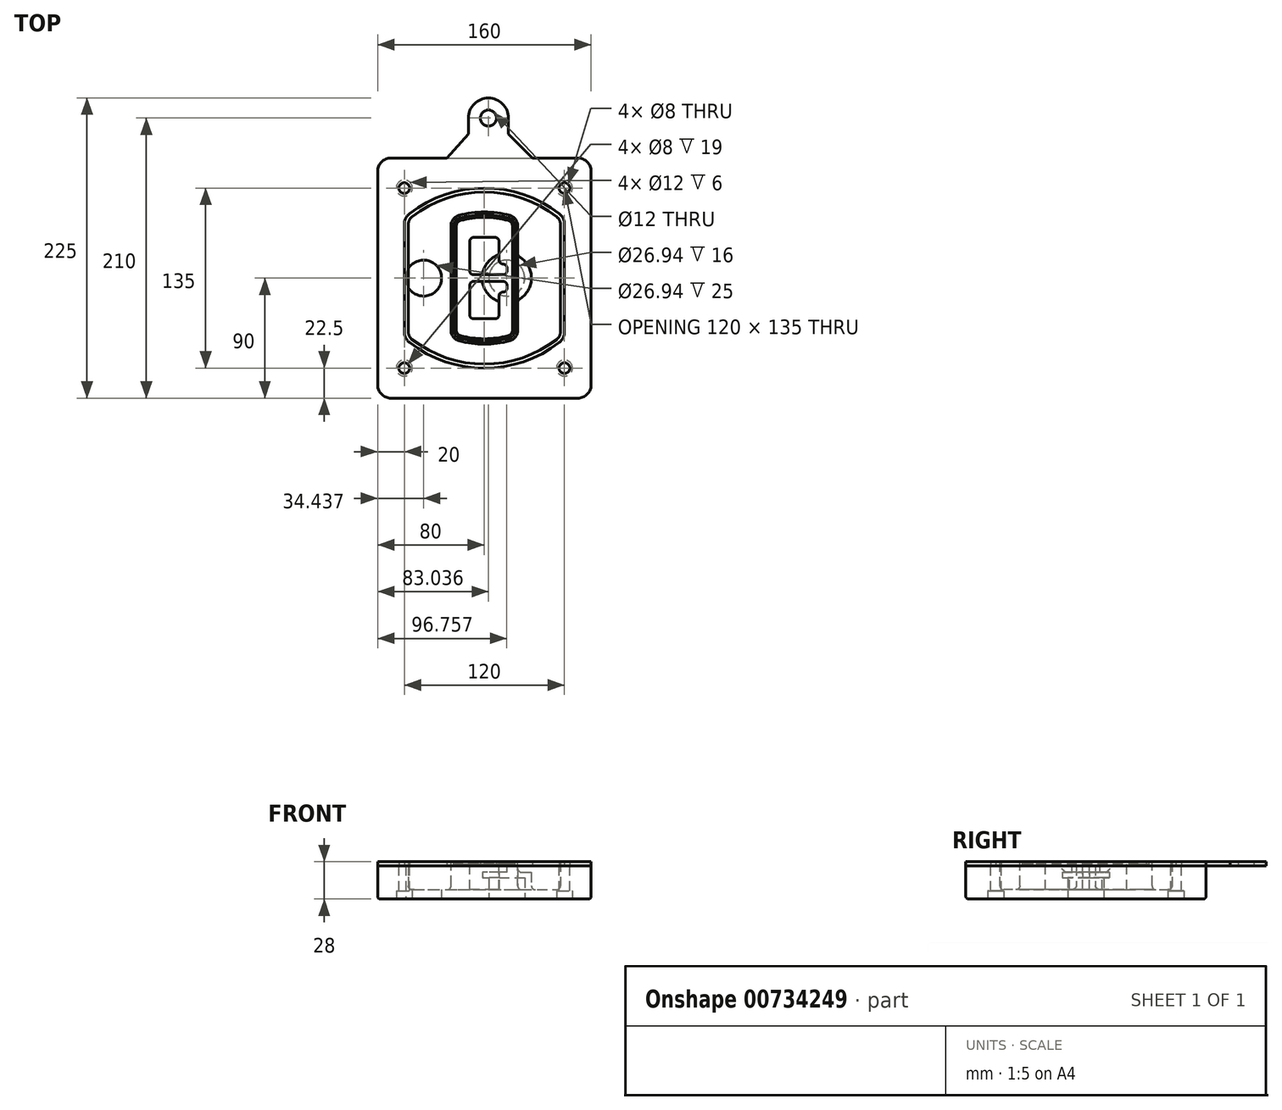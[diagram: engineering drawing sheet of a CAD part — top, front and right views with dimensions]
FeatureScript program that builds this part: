
annotation { "Feature Type Name" : "Feature", "Feature Type Description" : "" }
export const myFeature = defineFeature(function(context is Context, id is Id, definition is map)
    precondition{}
    {
        {
            var Q0;
            Q0=qCreatedBy(makeId("Top.planeOp"),FACE);
            var sketch = newSketch(context, id + "F0", { "sketchPlane" : qUnion([Q0])});
            skPoint(sketch, "E0.rect.middle", {"position": v(0, 0) * mm});
            skLineSegment(sketch, "E1.bottom", {"start": v(-70, -90) * mm, "end": v(70, -90) * mm});
            skLineSegment(sketch, "E1.top", {"start": v(-70, 90) * mm, "end": v(70, 90) * mm});
            skLineSegment(sketch, "E1.left", {"start": v(-80, -80) * mm, "end": v(-80, 80) * mm});
            skLineSegment(sketch, "E1.right", {"start": v(80, -80) * mm, "end": v(80, 80) * mm});
            skLineSegment(sketch, "E2", {"start": v(-80, 90) * mm, "end": v(80, -90) * mm, "construction": true});
            skLineSegment(sketch, "E3", {"start": v(80, 90) * mm, "end": v(-80, -90) * mm, "construction": true});
            skCircle(sketch, "E4", {"center": v(-60, 67.5) * mm, "radius": 4 * mm});
            skCircle(sketch, "E5", {"center": v(60, 67.5) * mm, "radius": 4 * mm});
            skCircle(sketch, "E6", {"center": v(60, -67.5) * mm, "radius": 4 * mm});
            skCircle(sketch, "E7", {"center": v(-60, -67.5) * mm, "radius": 4 * mm});
            skLineSegment(sketch, "E8", {"start": v(-60, 67.5) * mm, "end": v(60, 67.5) * mm, "construction": true});
            skLineSegment(sketch, "E9", {"start": v(60, 67.5) * mm, "end": v(60, -67.5) * mm, "construction": true});
            skLineSegment(sketch, "E10", {"start": v(60, -67.5) * mm, "end": v(-60, -67.5) * mm, "construction": true});
            skLineSegment(sketch, "E11", {"start": v(-60, -67.5) * mm, "end": v(-60, 67.5) * mm, "construction": true});
            skLineSegment(sketch, "E12", {"start": v(-60, 40.3) * mm, "end": v(-60, -40.3) * mm});
            skLineSegment(sketch, "E13", {"start": v(60, 40.3) * mm, "end": v(60, -40.3) * mm});
            skArc(sketch, "E14", {"start": v(56.15, 48.18) * mm, "mid": v(0, 67.5) * mm, "end": v(-56.15, 48.18) * mm});
            skArc(sketch, "E15", {"start": v(-56.15, -48.18) * mm, "mid": v(0, -67.5) * mm, "end": v(56.15, -48.18) * mm});
            skLineSegment(sketch, "E16", {"start": v(-60, 0) * mm, "end": v(60, 0) * mm, "construction": true});
            skPoint(sketch, "E17.visualSharp", {"position": v(-60, -45) * mm});
            skArc(sketch, "E17.filletArc", {"start": v(-60, -40.3) * mm, "mid": v(-58.99, -44.68) * mm, "end": v(-56.15, -48.18) * mm});
            skPoint(sketch, "E18.visualSharp", {"position": v(-60, 45) * mm});
            skArc(sketch, "E18.filletArc", {"start": v(-56.15, 48.18) * mm, "mid": v(-58.99, 44.68) * mm, "end": v(-60, 40.3) * mm});
            skPoint(sketch, "E19.visualSharp", {"position": v(60, 45) * mm});
            skArc(sketch, "E19.filletArc", {"start": v(60, 40.3) * mm, "mid": v(58.99, 44.68) * mm, "end": v(56.15, 48.18) * mm});
            skPoint(sketch, "E20.visualSharp", {"position": v(60, -45) * mm});
            skArc(sketch, "E20.filletArc", {"start": v(56.15, -48.18) * mm, "mid": v(58.99, -44.68) * mm, "end": v(60, -40.3) * mm});
            skPoint(sketch, "E21.visualSharp", {"position": v(-80, 90) * mm});
            skArc(sketch, "E21.filletArc", {"start": v(-70, 90) * mm, "mid": v(-77.07, 87.07) * mm, "end": v(-80, 80) * mm});
            skPoint(sketch, "E22.visualSharp", {"position": v(80, 90) * mm});
            skArc(sketch, "E22.filletArc", {"start": v(80, 80) * mm, "mid": v(77.07, 87.07) * mm, "end": v(70, 90) * mm});
            skPoint(sketch, "E23.visualSharp", {"position": v(80, -90) * mm});
            skArc(sketch, "E23.filletArc", {"start": v(70, -90) * mm, "mid": v(77.07, -87.07) * mm, "end": v(80, -80) * mm});
            skPoint(sketch, "E24.visualSharp", {"position": v(-80, -90) * mm});
            skArc(sketch, "E24.filletArc", {"start": v(-80, -80) * mm, "mid": v(-77.07, -87.07) * mm, "end": v(-70, -90) * mm});
            skArc(sketch, "E25.0", {"start": v(57, 40.3) * mm, "mid": v(56.3, 43.36) * mm, "end": v(54.3, 45.81) * mm});
            skLineSegment(sketch, "E25.1", {"start": v(57, 40.3) * mm, "end": v(57, -40.3) * mm});
            skArc(sketch, "E25.2", {"start": v(54.3, -45.81) * mm, "mid": v(56.3, -43.36) * mm, "end": v(57, -40.3) * mm});
            skArc(sketch, "E25.3", {"start": v(-54.3, -45.81) * mm, "mid": v(0, -64.5) * mm, "end": v(54.3, -45.81) * mm});
            skArc(sketch, "E25.4", {"start": v(-57, -40.3) * mm, "mid": v(-56.3, -43.36) * mm, "end": v(-54.3, -45.81) * mm});
            skArc(sketch, "E25.5", {"start": v(54.3, 45.81) * mm, "mid": v(0, 64.5) * mm, "end": v(-54.3, 45.81) * mm});
            skLineSegment(sketch, "E25.6", {"start": v(-57, 40.3) * mm, "end": v(-57, -40.3) * mm});
            skArc(sketch, "E25.7", {"start": v(-54.3, 45.81) * mm, "mid": v(-56.3, 43.36) * mm, "end": v(-57, 40.3) * mm});
            skArc(sketch, "E26.0", {"start": v(-58.62, 51.33) * mm, "mid": v(-62.58, 46.43) * mm, "end": v(-64, 40.3) * mm});
            skArc(sketch, "E26.1", {"start": v(58.62, 51.33) * mm, "mid": v(0, 71.5) * mm, "end": v(-58.62, 51.33) * mm});
            skArc(sketch, "E26.2", {"start": v(64, 40.3) * mm, "mid": v(62.58, 46.43) * mm, "end": v(58.62, 51.33) * mm});
            skLineSegment(sketch, "E26.3", {"start": v(64, 40.3) * mm, "end": v(64, -40.3) * mm});
            skArc(sketch, "E26.4", {"start": v(58.62, -51.33) * mm, "mid": v(62.58, -46.43) * mm, "end": v(64, -40.3) * mm});
            skLineSegment(sketch, "E26.5", {"start": v(-64, 40.3) * mm, "end": v(-64, -40.3) * mm});
            skArc(sketch, "E26.6", {"start": v(-58.62, -51.33) * mm, "mid": v(0, -71.5) * mm, "end": v(58.62, -51.33) * mm});
            skArc(sketch, "E26.7", {"start": v(-64, -40.3) * mm, "mid": v(-62.58, -46.43) * mm, "end": v(-58.62, -51.33) * mm});
            skSolve(sketch);
        }
        {
            var Q0;
            Q0=makeQuery(id+"F0.imprint","IMPRINT",FACE,{"disambiguationData":[TD([[makeQuery(id+"F0.imprint","IMPRINT",EDGE,{"derivedFrom":sQuery(id+"F0.wireOp",EDGE,"E1.bottom")}),1.0]])]});
            var Q1;
            Q1=makeQuery(id+"F0.imprint","IMPRINT",FACE,{"disambiguationData":[TD([[makeQuery(id+"F0.imprint","IMPRINT",EDGE,{"derivedFrom":sQuery(id+"F0.wireOp",EDGE,"E12")}),1.0]])]});
            var Q2;
            Q2=makeQuery(id+"F0.imprint","IMPRINT",FACE,{"disambiguationData":[TD([[makeQuery(id+"F0.imprint","IMPRINT",EDGE,{"derivedFrom":sQuery(id+"F0.wireOp",EDGE,"E25.0")}),1.0]])]});
            var Q3;
            Q3=makeQuery(id+"F0.imprint","IMPRINT",FACE,{"disambiguationData":[TD([[makeQuery(id+"F0.imprint","IMPRINT",EDGE,{"derivedFrom":sQuery(id+"F0.wireOp",EDGE,"E12")}),-1.0]])]});
            extrude(context, id + "F1", {"entities" : qUnion([Q0, Q1, Q2, Q3]), "oppositeDirection" : true, "depth" : 25 * mm});
        }
        {
            var Q0;
            Q0=makeQuery(id+"F0.imprint","IMPRINT",FACE,{"disambiguationData":[TD([[makeQuery(id+"F0.imprint","IMPRINT",EDGE,{"derivedFrom":sQuery(id+"F0.wireOp",EDGE,"E12")}),1.0]])]});
            extrude(context, id + "F2", {"entities" : qUnion([Q0]), "operationType" : NewBodyOperationType.ADD, "depth" : 3 * mm});
        }
        {
            var Q0;
            Q0=makeQuery(id+"F0.imprint","IMPRINT",FACE,{"disambiguationData":[TD([[makeQuery(id+"F0.imprint","IMPRINT",EDGE,{"derivedFrom":sQuery(id+"F0.wireOp",EDGE,"E25.0")}),1.0]])]});
            extrude(context, id + "F3", {"entities" : qUnion([Q0]), "operationType" : NewBodyOperationType.REMOVE, "oppositeDirection" : true, "depth" : 18 * mm});
        }
        {
            var Q0;
            Q0=makeQuery(id+"F2.opExtrude","CAP_FACE",FACE,{"disambiguationData":[OSD([sQuery(id+"F0.wireOp",EDGE,"E12"),sQuery(id+"F0.wireOp",EDGE,"E13"),sQuery(id+"F0.wireOp",EDGE,"E14"),sQuery(id+"F0.wireOp",EDGE,"E15"),sQuery(id+"F0.wireOp",EDGE,"E17.filletArc"),sQuery(id+"F0.wireOp",EDGE,"E18.filletArc"),sQuery(id+"F0.wireOp",EDGE,"E19.filletArc"),sQuery(id+"F0.wireOp",EDGE,"E20.filletArc"),sQuery(id+"F0.wireOp",EDGE,"E25.0"),sQuery(id+"F0.wireOp",EDGE,"E25.1"),sQuery(id+"F0.wireOp",EDGE,"E25.2"),sQuery(id+"F0.wireOp",EDGE,"E25.3"),sQuery(id+"F0.wireOp",EDGE,"E25.4"),sQuery(id+"F0.wireOp",EDGE,"E25.5"),sQuery(id+"F0.wireOp",EDGE,"E25.6"),sQuery(id+"F0.wireOp",EDGE,"E25.7")])],"isStart":false});
            var sketch = newSketch(context, id + "F4", { "sketchPlane" : qUnion([Q0])});
            skArc(sketch, "E27.0", {"start": v(-19.08, -46.97) * mm, "mid": v(0, -49.5) * mm, "end": v(19.08, -46.97) * mm});
            skArc(sketch, "E28.0", {"start": v(19.08, 46.97) * mm, "mid": v(0, 49.5) * mm, "end": v(-19.08, 46.97) * mm});
            skLineSegment(sketch, "E29", {"start": v(-25, 39.25) * mm, "end": v(-25, -39.25) * mm});
            skLineSegment(sketch, "E30", {"start": v(25, 39.25) * mm, "end": v(25, -39.25) * mm});
            skLineSegment(sketch, "E31", {"start": v(-25, 45.1) * mm, "end": v(25, 45.1) * mm, "construction": true});
            skLineSegment(sketch, "E32", {"start": v(-25, -45.1) * mm, "end": v(25, -45.1) * mm, "construction": true});
            skPoint(sketch, "E33.visualSharp", {"position": v(-25, 45.1) * mm});
            skArc(sketch, "E33.filletArc", {"start": v(-19.08, 46.97) * mm, "mid": v(-23.35, 44.11) * mm, "end": v(-25, 39.25) * mm});
            skPoint(sketch, "E34.visualSharp", {"position": v(25, 45.1) * mm});
            skArc(sketch, "E34.filletArc", {"start": v(25, 39.25) * mm, "mid": v(23.35, 44.11) * mm, "end": v(19.08, 46.97) * mm});
            skPoint(sketch, "E35.visualSharp", {"position": v(25, -45.1) * mm});
            skArc(sketch, "E35.filletArc", {"start": v(19.08, -46.97) * mm, "mid": v(23.35, -44.11) * mm, "end": v(25, -39.25) * mm});
            skPoint(sketch, "E36.visualSharp", {"position": v(-25, -45.1) * mm});
            skArc(sketch, "E36.filletArc", {"start": v(-25, -39.25) * mm, "mid": v(-23.35, -44.11) * mm, "end": v(-19.08, -46.97) * mm});
            skArc(sketch, "E37.0", {"start": v(54.3, 45.81) * mm, "mid": v(0, 64.5) * mm, "end": v(-54.3, 45.81) * mm});
            skArc(sketch, "E37.1", {"start": v(-54.3, 45.81) * mm, "mid": v(-56.3, 43.36) * mm, "end": v(-57, 40.3) * mm});
            skLineSegment(sketch, "E37.2", {"start": v(-57, 40.3) * mm, "end": v(-57, -40.3) * mm});
            skArc(sketch, "E37.3", {"start": v(-57, -40.3) * mm, "mid": v(-56.3, -43.36) * mm, "end": v(-54.3, -45.81) * mm});
            skArc(sketch, "E37.4", {"start": v(-54.3, -45.81) * mm, "mid": v(0, -64.5) * mm, "end": v(54.3, -45.81) * mm});
            skArc(sketch, "E37.5", {"start": v(54.3, -45.81) * mm, "mid": v(56.3, -43.36) * mm, "end": v(57, -40.3) * mm});
            skLineSegment(sketch, "E37.6", {"start": v(57, 40.3) * mm, "end": v(57, -40.3) * mm});
            skArc(sketch, "E37.7", {"start": v(57, 40.3) * mm, "mid": v(56.3, 43.36) * mm, "end": v(54.3, 45.81) * mm});
            skLineSegment(sketch, "E38.0", {"start": v(23, 39.25) * mm, "end": v(23, -39.25) * mm});
            skArc(sketch, "E38.1", {"start": v(18.56, -45.04) * mm, "mid": v(21.76, -42.9) * mm, "end": v(23, -39.25) * mm});
            skArc(sketch, "E38.2", {"start": v(-18.56, -45.04) * mm, "mid": v(0, -47.5) * mm, "end": v(18.56, -45.04) * mm});
            skArc(sketch, "E38.3", {"start": v(-23, -39.25) * mm, "mid": v(-21.76, -42.9) * mm, "end": v(-18.56, -45.04) * mm});
            skLineSegment(sketch, "E38.4", {"start": v(-23, 39.25) * mm, "end": v(-23, -39.25) * mm});
            skArc(sketch, "E38.5", {"start": v(23, 39.25) * mm, "mid": v(21.76, 42.9) * mm, "end": v(18.56, 45.04) * mm});
            skArc(sketch, "E38.6", {"start": v(-18.56, 45.04) * mm, "mid": v(-21.76, 42.9) * mm, "end": v(-23, 39.25) * mm});
            skArc(sketch, "E38.7", {"start": v(18.56, 45.04) * mm, "mid": v(0, 47.5) * mm, "end": v(-18.56, 45.04) * mm});
            skArc(sketch, "E39.0", {"start": v(21, 39.25) * mm, "mid": v(20.18, 41.68) * mm, "end": v(18.04, 43.1) * mm});
            skLineSegment(sketch, "E39.1", {"start": v(21, 39.25) * mm, "end": v(21, -39.25) * mm});
            skArc(sketch, "E39.2", {"start": v(18.04, -43.1) * mm, "mid": v(20.18, -41.68) * mm, "end": v(21, -39.25) * mm});
            skArc(sketch, "E39.3", {"start": v(-18.04, -43.1) * mm, "mid": v(0, -45.5) * mm, "end": v(18.04, -43.1) * mm});
            skArc(sketch, "E39.4", {"start": v(-21, -39.25) * mm, "mid": v(-20.18, -41.68) * mm, "end": v(-18.04, -43.1) * mm});
            skArc(sketch, "E39.5", {"start": v(18.04, 43.1) * mm, "mid": v(0, 45.5) * mm, "end": v(-18.04, 43.1) * mm});
            skLineSegment(sketch, "E39.6", {"start": v(-21, 39.25) * mm, "end": v(-21, -39.25) * mm});
            skArc(sketch, "E39.7", {"start": v(-18.04, 43.1) * mm, "mid": v(-20.18, 41.68) * mm, "end": v(-21, 39.25) * mm});
            skLineSegment(sketch, "E40", {"start": v(-25, 0) * mm, "end": v(25, 0) * mm, "construction": true});
            skLineSegment(sketch, "E41", {"start": v(-11, 5.5) * mm, "end": v(-11, 27.5) * mm});
            skLineSegment(sketch, "E42", {"start": v(-8, 30.5) * mm, "end": v(8, 30.5) * mm});
            skLineSegment(sketch, "E43", {"start": v(11, 27.5) * mm, "end": v(11, 13.5) * mm});
            skLineSegment(sketch, "E44", {"start": v(14, 10.5) * mm, "end": v(14, 10.5) * mm});
            skLineSegment(sketch, "E45", {"start": v(17, 7.5) * mm, "end": v(17, 5.5) * mm});
            skLineSegment(sketch, "E46", {"start": v(14, 2.5) * mm, "end": v(-8, 2.5) * mm});
            skPoint(sketch, "E47.visualSharp", {"position": v(-11, 30.5) * mm});
            skArc(sketch, "E47.filletArc", {"start": v(-8, 30.5) * mm, "mid": v(-10.12, 29.62) * mm, "end": v(-11, 27.5) * mm});
            skPoint(sketch, "E48.visualSharp", {"position": v(11, 30.5) * mm});
            skArc(sketch, "E48.filletArc", {"start": v(11, 27.5) * mm, "mid": v(10.12, 29.62) * mm, "end": v(8, 30.5) * mm});
            skPoint(sketch, "E49.visualSharp", {"position": v(11, 10.5) * mm});
            skArc(sketch, "E49.filletArc", {"start": v(11, 13.5) * mm, "mid": v(11.88, 11.38) * mm, "end": v(14, 10.5) * mm});
            skPoint(sketch, "E50.visualSharp", {"position": v(17, 10.5) * mm});
            skArc(sketch, "E50.filletArc", {"start": v(17, 7.5) * mm, "mid": v(16.12, 9.62) * mm, "end": v(14, 10.5) * mm});
            skPoint(sketch, "E51.visualSharp", {"position": v(17, 2.5) * mm});
            skArc(sketch, "E51.filletArc", {"start": v(14, 2.5) * mm, "mid": v(16.12, 3.38) * mm, "end": v(17, 5.5) * mm});
            skPoint(sketch, "E52.visualSharp", {"position": v(-11, 2.5) * mm});
            skArc(sketch, "E52.filletArc", {"start": v(-11, 5.5) * mm, "mid": v(-10.12, 3.38) * mm, "end": v(-8, 2.5) * mm});
            skLineSegment(sketch, "E53.0.MirrorCS", {"start": v(14, -2.5) * mm, "end": v(-8, -2.5) * mm});
            skArc(sketch, "E54.0.MirrorCS", {"start": v(-11, -5.5) * mm, "mid": v(-10.12, -3.38) * mm, "end": v(-8, -2.5) * mm});
            skLineSegment(sketch, "E55.0.MirrorCS", {"start": v(-11, -5.5) * mm, "end": v(-11, -27.5) * mm});
            skArc(sketch, "E56.0.MirrorCS", {"start": v(-8, -30.5) * mm, "mid": v(-10.12, -29.62) * mm, "end": v(-11, -27.5) * mm});
            skLineSegment(sketch, "E57.0.MirrorCS", {"start": v(-8, -30.5) * mm, "end": v(8, -30.5) * mm});
            skArc(sketch, "E58.0.MirrorCS", {"start": v(11, -27.5) * mm, "mid": v(10.12, -29.62) * mm, "end": v(8, -30.5) * mm});
            skLineSegment(sketch, "E59.0.MirrorCS", {"start": v(11, -27.5) * mm, "end": v(11, -13.5) * mm});
            skArc(sketch, "E60.0.MirrorCS", {"start": v(11, -13.5) * mm, "mid": v(11.88, -11.38) * mm, "end": v(14, -10.5) * mm});
            skArc(sketch, "E61.0.MirrorCS", {"start": v(17, -7.5) * mm, "mid": v(16.12, -9.62) * mm, "end": v(14, -10.5) * mm});
            skLineSegment(sketch, "E62.0.MirrorCS", {"start": v(17, -7.5) * mm, "end": v(17, -5.5) * mm});
            skArc(sketch, "E63.0.MirrorCS", {"start": v(14, -2.5) * mm, "mid": v(16.12, -3.38) * mm, "end": v(17, -5.5) * mm});
            skSolve(sketch);
        }
        {
            var Q0;
            Q0=makeQuery(id+"F4.imprint","IMPRINT",FACE,{"disambiguationData":[TD([[makeQuery(id+"F4.imprint","IMPRINT",EDGE,{"derivedFrom":sQuery(id+"F4.wireOp",EDGE,"E27.0")}),1.0]])]});
            var Q1;
            Q1=makeQuery(id+"F4.imprint","IMPRINT",FACE,{"disambiguationData":[TD([[makeQuery(id+"F4.imprint","IMPRINT",EDGE,{"derivedFrom":sQuery(id+"F4.wireOp",EDGE,"E38.0")}),-1.0]])]});
            var Q2;
            Q2=makeQuery(id+"F4.imprint","IMPRINT",FACE,{"disambiguationData":[TD([[makeQuery(id+"F4.imprint","IMPRINT",EDGE,{"derivedFrom":sQuery(id+"F4.wireOp",EDGE,"E39.0")}),1.0]])]});
            extrude(context, id + "F5", {"entities" : qUnion([Q0, Q1, Q2]), "operationType" : NewBodyOperationType.ADD, "endBound" : BoundingType.UP_TO_NEXT, "oppositeDirection" : true, "depth" : 25 * mm});
        }
        {
            var Q0;
            Q0=makeQuery(id+"F4.imprint","IMPRINT",FACE,{"disambiguationData":[TD([[makeQuery(id+"F4.imprint","IMPRINT",EDGE,{"derivedFrom":sQuery(id+"F4.wireOp",EDGE,"E38.0")}),-1.0]])]});
            extrude(context, id + "F6", {"entities" : qUnion([Q0]), "operationType" : NewBodyOperationType.REMOVE, "oppositeDirection" : true, "depth" : 2 * mm});
        }
        {
            var Q0;
            Q0=makeQuery(id+"F1.opExtrude","CAP_FACE",FACE,{"disambiguationData":[OSD([sQuery(id+"F0.wireOp",EDGE,"E1.bottom"),sQuery(id+"F0.wireOp",EDGE,"E1.top"),sQuery(id+"F0.wireOp",EDGE,"E1.left"),sQuery(id+"F0.wireOp",EDGE,"E1.right"),sQuery(id+"F0.wireOp",EDGE,"E4"),sQuery(id+"F0.wireOp",EDGE,"E5"),sQuery(id+"F0.wireOp",EDGE,"E6"),sQuery(id+"F0.wireOp",EDGE,"E7"),sQuery(id+"F0.wireOp",EDGE,"E21.filletArc"),sQuery(id+"F0.wireOp",EDGE,"E22.filletArc"),sQuery(id+"F0.wireOp",EDGE,"E23.filletArc"),sQuery(id+"F0.wireOp",EDGE,"E24.filletArc")])],"isStart":false});
            var sketch = newSketch(context, id + "F7", { "sketchPlane" : qUnion([Q0])});
            skCircle(sketch, "E64", {"center": v(16.76, 0) * mm, "radius": 13.47 * mm});
            skCircle(sketch, "E65", {"center": v(-45.56, 0) * mm, "radius": 13.47 * mm});
            skLineSegment(sketch, "E66", {"start": v(80, 0) * mm, "end": v(-80, 0) * mm});
            skCircle(sketch, "E67", {"center": v(16.76, 0) * mm, "radius": 18.47 * mm});
            skCircle(sketch, "E68", {"center": v(60, -67.5) * mm, "radius": 6 * mm});
            skCircle(sketch, "E69", {"center": v(-60, -67.5) * mm, "radius": 6 * mm});
            skCircle(sketch, "E70", {"center": v(-60, 67.5) * mm, "radius": 6 * mm});
            skCircle(sketch, "E71", {"center": v(60, 67.5) * mm, "radius": 6 * mm});
            skSolve(sketch);
        }
        {
            var Q0;
            {var subQ1=sQuery(id+"F7.wireOp",EDGE,"E66");var subQ4=sQuery(id+"F7.wireOp",EDGE,"E64");var subQ6=makeQuery(id+"F7.imprint","INTERSECT",VERTEX,{"disambiguationData":[OD(0.0)],"derivedFrom":[subQ4,subQ1]});Q0=makeQuery(id+"F7.imprint","IMPRINT",FACE,{"disambiguationData":[TD([[makeQuery(id+"F7.imprint","IMPRINT",EDGE,{"disambiguationData":[TD([[subQ6,-1.0]])],"derivedFrom":subQ4}),-1.0]])]});}
            var Q1;
            {var subQ0=sQuery(id+"F7.wireOp",EDGE,"E66");var subQ1=sQuery(id+"F7.wireOp",EDGE,"E64");var subQ3=makeQuery(id+"F7.imprint","INTERSECT",VERTEX,{"disambiguationData":[OD(0.0)],"derivedFrom":[subQ1,subQ0]});Q1=makeQuery(id+"F7.imprint","IMPRINT",FACE,{"disambiguationData":[TD([[makeQuery(id+"F7.imprint","IMPRINT",EDGE,{"disambiguationData":[TD([[subQ3,-1.0]])],"derivedFrom":subQ1}),1.0]])]});}
            var Q2;
            {var subQ0=sQuery(id+"F7.wireOp",EDGE,"E66");var subQ1=sQuery(id+"F7.wireOp",EDGE,"E64");var subQ3=makeQuery(id+"F7.imprint","INTERSECT",VERTEX,{"disambiguationData":[OD(0.0)],"derivedFrom":[subQ1,subQ0]});Q2=makeQuery(id+"F7.imprint","IMPRINT",FACE,{"disambiguationData":[TD([[makeQuery(id+"F7.imprint","IMPRINT",EDGE,{"disambiguationData":[TD([[subQ3,1.0]])],"derivedFrom":subQ1}),1.0]])]});}
            var Q3;
            {var subQ1=sQuery(id+"F7.wireOp",EDGE,"E66");var subQ4=sQuery(id+"F7.wireOp",EDGE,"E64");var subQ6=makeQuery(id+"F7.imprint","INTERSECT",VERTEX,{"disambiguationData":[OD(0.0)],"derivedFrom":[subQ4,subQ1]});Q3=makeQuery(id+"F7.imprint","IMPRINT",FACE,{"disambiguationData":[TD([[makeQuery(id+"F7.imprint","IMPRINT",EDGE,{"disambiguationData":[TD([[subQ6,1.0]])],"derivedFrom":subQ4}),-1.0]])]});}
            extrude(context, id + "F8", {"entities" : qUnion([Q0, Q1, Q2, Q3]), "operationType" : NewBodyOperationType.ADD, "oppositeDirection" : true, "depth" : 20 * mm});
        }
        {
            var Q0;
            {var subQ0=sQuery(id+"F7.wireOp",EDGE,"E66");var subQ1=sQuery(id+"F7.wireOp",EDGE,"E64");var subQ3=makeQuery(id+"F7.imprint","INTERSECT",VERTEX,{"disambiguationData":[OD(0.0)],"derivedFrom":[subQ1,subQ0]});Q0=makeQuery(id+"F7.imprint","IMPRINT",FACE,{"disambiguationData":[TD([[makeQuery(id+"F7.imprint","IMPRINT",EDGE,{"disambiguationData":[TD([[subQ3,-1.0]])],"derivedFrom":subQ1}),1.0]])]});}
            var Q1;
            {var subQ0=sQuery(id+"F7.wireOp",EDGE,"E66");var subQ1=sQuery(id+"F7.wireOp",EDGE,"E64");var subQ3=makeQuery(id+"F7.imprint","INTERSECT",VERTEX,{"disambiguationData":[OD(0.0)],"derivedFrom":[subQ1,subQ0]});Q1=makeQuery(id+"F7.imprint","IMPRINT",FACE,{"disambiguationData":[TD([[makeQuery(id+"F7.imprint","IMPRINT",EDGE,{"disambiguationData":[TD([[subQ3,1.0]])],"derivedFrom":subQ1}),1.0]])]});}
            extrude(context, id + "F9", {"entities" : qUnion([Q0, Q1]), "operationType" : NewBodyOperationType.REMOVE, "oppositeDirection" : true, "depth" : 16 * mm});
        }
        {
            var Q0;
            {var subQ0=sQuery(id+"F7.wireOp",EDGE,"E66");var subQ1=sQuery(id+"F7.wireOp",EDGE,"E65");var subQ3=makeQuery(id+"F7.imprint","INTERSECT",VERTEX,{"disambiguationData":[OD(0.0)],"derivedFrom":[subQ1,subQ0]});Q0=makeQuery(id+"F7.imprint","IMPRINT",FACE,{"disambiguationData":[TD([[makeQuery(id+"F7.imprint","IMPRINT",EDGE,{"disambiguationData":[TD([[subQ3,-1.0]])],"derivedFrom":subQ1}),1.0]])]});}
            var Q1;
            {var subQ0=sQuery(id+"F7.wireOp",EDGE,"E66");var subQ1=sQuery(id+"F7.wireOp",EDGE,"E65");var subQ3=makeQuery(id+"F7.imprint","INTERSECT",VERTEX,{"disambiguationData":[OD(0.0)],"derivedFrom":[subQ1,subQ0]});Q1=makeQuery(id+"F7.imprint","IMPRINT",FACE,{"disambiguationData":[TD([[makeQuery(id+"F7.imprint","IMPRINT",EDGE,{"disambiguationData":[TD([[subQ3,1.0]])],"derivedFrom":subQ1}),1.0]])]});}
            extrude(context, id + "F10", {"entities" : qUnion([Q0, Q1]), "operationType" : NewBodyOperationType.REMOVE, "oppositeDirection" : true, "depth" : 25 * mm});
        }
        {
            var Q0;
            Q0=makeQuery(id+"F7.imprint","IMPRINT",FACE,{"disambiguationData":[TD([[makeQuery(id+"F7.imprint","IMPRINT",EDGE,{"derivedFrom":sQuery(id+"F7.wireOp",EDGE,"E68")}),1.0]])]});
            var Q1;
            Q1=makeQuery(id+"F7.imprint","IMPRINT",FACE,{"disambiguationData":[TD([[makeQuery(id+"F7.imprint","IMPRINT",EDGE,{"derivedFrom":makeQuery(id+"F1.opExtrude","CAP_EDGE",EDGE,{"disambiguationData":[OSD([sQuery(id+"F0.wireOp",EDGE,"E5")])],"isStart":false})}),-1.0]])]});
            var Q2;
            Q2=makeQuery(id+"F7.imprint","IMPRINT",FACE,{"disambiguationData":[TD([[makeQuery(id+"F7.imprint","IMPRINT",EDGE,{"derivedFrom":sQuery(id+"F7.wireOp",EDGE,"E69")}),1.0]])]});
            var Q3;
            Q3=makeQuery(id+"F7.imprint","IMPRINT",FACE,{"disambiguationData":[TD([[makeQuery(id+"F7.imprint","IMPRINT",EDGE,{"derivedFrom":makeQuery(id+"F1.opExtrude","CAP_EDGE",EDGE,{"disambiguationData":[OSD([sQuery(id+"F0.wireOp",EDGE,"E4")])],"isStart":false})}),-1.0]])]});
            var Q4;
            Q4=makeQuery(id+"F7.imprint","IMPRINT",FACE,{"disambiguationData":[TD([[makeQuery(id+"F7.imprint","IMPRINT",EDGE,{"derivedFrom":sQuery(id+"F7.wireOp",EDGE,"E70")}),1.0]])]});
            var Q5;
            Q5=makeQuery(id+"F7.imprint","IMPRINT",FACE,{"disambiguationData":[TD([[makeQuery(id+"F7.imprint","IMPRINT",EDGE,{"derivedFrom":makeQuery(id+"F1.opExtrude","CAP_EDGE",EDGE,{"disambiguationData":[OSD([sQuery(id+"F0.wireOp",EDGE,"E7")])],"isStart":false})}),-1.0]])]});
            var Q6;
            Q6=makeQuery(id+"F7.imprint","IMPRINT",FACE,{"disambiguationData":[TD([[makeQuery(id+"F7.imprint","IMPRINT",EDGE,{"derivedFrom":sQuery(id+"F7.wireOp",EDGE,"E71")}),1.0]])]});
            var Q7;
            Q7=makeQuery(id+"F7.imprint","IMPRINT",FACE,{"disambiguationData":[TD([[makeQuery(id+"F7.imprint","IMPRINT",EDGE,{"derivedFrom":makeQuery(id+"F1.opExtrude","CAP_EDGE",EDGE,{"disambiguationData":[OSD([sQuery(id+"F0.wireOp",EDGE,"E6")])],"isStart":false})}),-1.0]])]});
            extrude(context, id + "F11", {"entities" : qUnion([Q0, Q1, Q2, Q3, Q4, Q5, Q6, Q7]), "operationType" : NewBodyOperationType.REMOVE, "oppositeDirection" : true, "depth" : 6 * mm});
        }
        {
            var Q0;
            Q0=makeQuery(id+"F9.boolean.opBoolean","COPY",FACE,{"derivedFrom":makeQuery(id+"F9.opExtrude","CAP_FACE",FACE,{"disambiguationData":[OSD([sQuery(id+"F7.wireOp",EDGE,"E64")])],"isStart":false})});
            var sketch = newSketch(context, id + "F12", { "sketchPlane" : qUnion([Q0])});
            skArc(sketch, "E72.0", {"start": v(11, 17.55) * mm, "mid": v(2.57, 11.82) * mm, "end": v(-1.54, 2.5) * mm});
            skArc(sketch, "E72.1", {"start": v(-1.54, -2.5) * mm, "mid": v(2.57, -11.82) * mm, "end": v(11, -17.55) * mm});
            skLineSegment(sketch, "E73", {"start": v(-1.54, -2.5) * mm, "end": v(14, -2.5) * mm});
            skLineSegment(sketch, "E74.0", {"start": v(14, 2.5) * mm, "end": v(-1.54, 2.5) * mm});
            skArc(sketch, "E74.1", {"start": v(14, 2.5) * mm, "mid": v(16.12, 3.38) * mm, "end": v(17, 5.5) * mm});
            skLineSegment(sketch, "E74.2", {"start": v(17, 7.5) * mm, "end": v(17, 5.5) * mm});
            skArc(sketch, "E74.3", {"start": v(17, 7.5) * mm, "mid": v(16.12, 9.62) * mm, "end": v(14, 10.5) * mm});
            skArc(sketch, "E74.4", {"start": v(11, 13.5) * mm, "mid": v(11.88, 11.38) * mm, "end": v(14, 10.5) * mm});
            skLineSegment(sketch, "E74.5", {"start": v(11, 17.55) * mm, "end": v(11, 13.5) * mm});
            skLineSegment(sketch, "E74.7", {"start": v(14, -2.5) * mm, "end": v(-1.54, -2.5) * mm});
            skArc(sketch, "E74.8", {"start": v(14, -2.5) * mm, "mid": v(16.12, -3.38) * mm, "end": v(17, -5.5) * mm});
            skLineSegment(sketch, "E74.9", {"start": v(17, -7.5) * mm, "end": v(17, -5.5) * mm});
            skArc(sketch, "E74.10", {"start": v(17, -7.5) * mm, "mid": v(16.12, -9.62) * mm, "end": v(14, -10.5) * mm});
            skArc(sketch, "E74.11", {"start": v(11, -13.5) * mm, "mid": v(11.88, -11.38) * mm, "end": v(14, -10.5) * mm});
            skLineSegment(sketch, "E74.12", {"start": v(11, -17.55) * mm, "end": v(11, -13.5) * mm});
            skPoint(sketch, "E75.orphan", {"position": v(11, -27.5) * mm});
            skPoint(sketch, "E76.orphan", {"position": v(-8, -2.5) * mm});
            skPoint(sketch, "E77.orphan", {"position": v(-8, 2.5) * mm});
            skPoint(sketch, "E78.orphan", {"position": v(11, 27.5) * mm});
            skSolve(sketch);
        }
        {
            var Q0;
            {var subQ7=sQuery(id+"F12.wireOp",EDGE,"E72.0");var subQ14=sQuery(id+"F12.wireOp",EDGE,"E72.1");var subQ16=sQuery(id+"F12.wireOp",EDGE,"E74.1");var subQ18=sQuery(id+"F12.wireOp",EDGE,"E74.8");Q0=qUnion([makeQuery(id+"F12.imprint","IMPRINT",FACE,{"disambiguationData":[TD([[makeQuery(id+"F12.imprint","IMPRINT",EDGE,{"derivedFrom":subQ7}),1.0]])]}),makeQuery(id+"F12.imprint","IMPRINT",FACE,{"disambiguationData":[TD([[makeQuery(id+"F12.imprint","IMPRINT",EDGE,{"derivedFrom":subQ14}),1.0]])]}),makeQuery(id+"F12.imprint","IMPRINT",FACE,{"disambiguationData":[TD([[makeQuery(id+"F12.imprint","IMPRINT",EDGE,{"derivedFrom":subQ16}),1.0]])]}),makeQuery(id+"F12.imprint","IMPRINT",FACE,{"disambiguationData":[TD([[makeQuery(id+"F12.imprint","IMPRINT",EDGE,{"derivedFrom":subQ18}),-1.0]])]})]);}
            var Q1;
            Q1=makeQuery(id+"F5.boolean.opBoolean","SPLIT",FACE,{"disambiguationData":[TD([makeQuery(id+"F5.opExtrude","SWEPT_FACE",FACE,{"disambiguationData":[OSD([sQuery(id+"F4.wireOp",EDGE,"E41")])]})])],"derivedFrom":makeQuery(id+"F3.boolean.opBoolean","COPY",FACE,{"derivedFrom":makeQuery(id+"F3.opExtrude","CAP_FACE",FACE,{"disambiguationData":[OSD([sQuery(id+"F0.wireOp",EDGE,"E25.0"),sQuery(id+"F0.wireOp",EDGE,"E25.1"),sQuery(id+"F0.wireOp",EDGE,"E25.2"),sQuery(id+"F0.wireOp",EDGE,"E25.3"),sQuery(id+"F0.wireOp",EDGE,"E25.4"),sQuery(id+"F0.wireOp",EDGE,"E25.5"),sQuery(id+"F0.wireOp",EDGE,"E25.6"),sQuery(id+"F0.wireOp",EDGE,"E25.7")])],"isStart":false})})});
            extrude(context, id + "F13", {"entities" : qUnion([Q0]), "operationType" : NewBodyOperationType.REMOVE, "endBound" : BoundingType.UP_TO_SURFACE, "endBoundEntityFace" : qUnion([Q1]), "depth" : 25 * mm});
        }
        {
            var Q0;
            Q0=makeQuery(id+"F3.boolean.opBoolean","COPY",EDGE,{"derivedFrom":makeQuery(id+"F3.opExtrude","CAP_EDGE",EDGE,{"disambiguationData":[OSD([sQuery(id+"F0.wireOp",EDGE,"E25.6")])],"isStart":false})});
            var Q1;
            Q1=makeQuery(id+"F8.boolean.opBoolean","INTERSECT",EDGE,{"derivedFrom":[makeQuery(id+"F5.opExtrude","SWEPT_FACE",FACE,{"disambiguationData":[OSD([sQuery(id+"F4.wireOp",EDGE,"E30")])]}),makeQuery(id+"F8.opExtrude","CAP_FACE",FACE,{"disambiguationData":[OSD([sQuery(id+"F7.wireOp",EDGE,"E67")])],"isStart":false})]});
            var Q2;
            Q2=makeQuery(id+"F8.boolean.opBoolean","INTERSECT",EDGE,{"disambiguationData":[OD(1.0)],"derivedFrom":[makeQuery(id+"F5.opExtrude","SWEPT_FACE",FACE,{"disambiguationData":[OSD([sQuery(id+"F4.wireOp",EDGE,"E30")])]}),makeQuery(id+"F8.opExtrude","SWEPT_FACE",FACE,{"disambiguationData":[OSD([sQuery(id+"F7.wireOp",EDGE,"E67")])]})]});
            var Q3;
            {var subQ0=sQuery(id+"F4.wireOp",EDGE,"E30");Q3=makeQuery(id+"F8.boolean.opBoolean","SPLIT",EDGE,{"disambiguationData":[TD([makeQuery(id+"F5.opExtrude","SWEPT_FACE",FACE,{"disambiguationData":[OSD([sQuery(id+"F4.wireOp",EDGE,"E35.filletArc")])]})])],"derivedFrom":makeQuery(id+"F5.opExtrude","CAP_EDGE",EDGE,{"disambiguationData":[OSD([subQ0])],"isStart":false})});}
            var Q4;
            {var subQ0=sQuery(id+"F0.wireOp",EDGE,"E25.7");var subQ1=sQuery(id+"F0.wireOp",EDGE,"E25.1");var subQ2=sQuery(id+"F0.wireOp",EDGE,"E25.6");var subQ3=sQuery(id+"F0.wireOp",EDGE,"E25.5");var subQ4=sQuery(id+"F0.wireOp",EDGE,"E25.4");var subQ5=sQuery(id+"F0.wireOp",EDGE,"E25.0");var subQ6=sQuery(id+"F0.wireOp",EDGE,"E25.2");var subQ7=sQuery(id+"F0.wireOp",EDGE,"E25.3");Q4=makeQuery(id+"F8.boolean.opBoolean","INTERSECT",EDGE,{"derivedFrom":[makeQuery(id+"F5.boolean.opBoolean","SPLIT",FACE,{"disambiguationData":[TD([makeQuery(id+"F2.opExtrude","SWEPT_FACE",FACE,{"disambiguationData":[OSD([subQ5])]})])],"derivedFrom":makeQuery(id+"F3.boolean.opBoolean","COPY",FACE,{"derivedFrom":makeQuery(id+"F3.opExtrude","CAP_FACE",FACE,{"disambiguationData":[OSD([subQ5,subQ1,subQ6,subQ7,subQ4,subQ3,subQ2,subQ0])],"isStart":false})})}),makeQuery(id+"F8.opExtrude","SWEPT_FACE",FACE,{"disambiguationData":[OSD([sQuery(id+"F7.wireOp",EDGE,"E67")])]})]});}
            var Q5;
            Q5=makeQuery(id+"F8.boolean.opBoolean","INTERSECT",EDGE,{"disambiguationData":[OD(0.0)],"derivedFrom":[makeQuery(id+"F5.opExtrude","SWEPT_FACE",FACE,{"disambiguationData":[OSD([sQuery(id+"F4.wireOp",EDGE,"E30")])]}),makeQuery(id+"F8.opExtrude","SWEPT_FACE",FACE,{"disambiguationData":[OSD([sQuery(id+"F7.wireOp",EDGE,"E67")])]})]});
            fillet(context, id + "F14", {"entities" : qUnion([Q0, Q1, Q2, Q3, Q4, Q5]), "radius" : 3 * mm, "tangentPropagation" : true, "allowEdgeOverflow" : false});
        }
        {
            var Q0;
            Q0=makeQuery(id+"F1.opExtrude","CAP_EDGE",EDGE,{"disambiguationData":[OSD([sQuery(id+"F0.wireOp",EDGE,"E1.bottom")])],"isStart":false});
            fillet(context, id + "F15", {"entities" : qUnion([Q0]), "radius" : 2 * mm, "tangentPropagation" : true, "allowEdgeOverflow" : false});
        }
        {
            var Q0;
            {var subQ0=sQuery(id+"F0.wireOp",EDGE,"E21.filletArc");var subQ1=sQuery(id+"F0.wireOp",EDGE,"E7");var subQ2=sQuery(id+"F0.wireOp",EDGE,"E6");var subQ3=sQuery(id+"F0.wireOp",EDGE,"E5");var subQ4=sQuery(id+"F0.wireOp",EDGE,"E4");var subQ5=sQuery(id+"F0.wireOp",EDGE,"E22.filletArc");var subQ6=sQuery(id+"F0.wireOp",EDGE,"E1.bottom");var subQ7=sQuery(id+"F0.wireOp",EDGE,"E1.right");var subQ8=sQuery(id+"F0.wireOp",EDGE,"E1.top");var subQ9=sQuery(id+"F0.wireOp",EDGE,"E1.left");var subQ10=sQuery(id+"F0.wireOp",EDGE,"E23.filletArc");var subQ11=sQuery(id+"F0.wireOp",EDGE,"E24.filletArc");Q0=makeQuery(id+"F2.boolean.opBoolean","SPLIT",FACE,{"disambiguationData":[TD([makeQuery(id+"F1.opExtrude","SWEPT_FACE",FACE,{"disambiguationData":[OSD([subQ6])]})])],"derivedFrom":makeQuery(id+"F1.opExtrude","CAP_FACE",FACE,{"disambiguationData":[OSD([subQ6,subQ8,subQ9,subQ7,subQ4,subQ3,subQ2,subQ1,subQ0,subQ5,subQ10,subQ11])],"isStart":true})});}
            var sketch = newSketch(context, id + "F16", { "sketchPlane" : qUnion([Q0])});
            skArc(sketch, "E79.1", {"start": v(80, 80) * mm, "mid": v(77.07, 87.07) * mm, "end": v(70, 90) * mm});
            skArc(sketch, "E79.2", {"start": v(-70, 90) * mm, "mid": v(-77.07, 87.07) * mm, "end": v(-80, 80) * mm});
            skLineSegment(sketch, "E79.3", {"start": v(-80, -80) * mm, "end": v(-80, 80) * mm});
            skArc(sketch, "E79.4", {"start": v(-80, -80) * mm, "mid": v(-77.07, -87.07) * mm, "end": v(-70, -90) * mm});
            skLineSegment(sketch, "E79.5", {"start": v(-70, -90) * mm, "end": v(70, -90) * mm});
            skArc(sketch, "E79.6", {"start": v(70, -90) * mm, "mid": v(77.07, -87.07) * mm, "end": v(80, -80) * mm});
            skLineSegment(sketch, "E79.7", {"start": v(80, -80) * mm, "end": v(80, 80) * mm});
            skArc(sketch, "E79.8", {"start": v(56.15, 48.18) * mm, "mid": v(0, 67.5) * mm, "end": v(-56.15, 48.18) * mm});
            skLineSegment(sketch, "E79.9", {"start": v(60, 40.3) * mm, "end": v(60, -40.3) * mm});
            skArc(sketch, "E79.10", {"start": v(-56.15, -48.18) * mm, "mid": v(0, -67.5) * mm, "end": v(56.15, -48.18) * mm});
            skLineSegment(sketch, "E79.11", {"start": v(-60, 40.3) * mm, "end": v(-60, -40.3) * mm});
            skArc(sketch, "E79.12", {"start": v(-56.15, 48.18) * mm, "mid": v(-58.99, 44.68) * mm, "end": v(-60, 40.3) * mm});
            skCircle(sketch, "E79.13", {"center": v(60, -67.5) * mm, "radius": 4 * mm});
            skCircle(sketch, "E79.14", {"center": v(60, 67.5) * mm, "radius": 4 * mm});
            skCircle(sketch, "E79.15", {"center": v(-60, 67.5) * mm, "radius": 4 * mm});
            skCircle(sketch, "E79.16", {"center": v(-60, -67.5) * mm, "radius": 4 * mm});
            skArc(sketch, "E79.17", {"start": v(60, 40.3) * mm, "mid": v(58.99, 44.68) * mm, "end": v(56.15, 48.18) * mm});
            skPoint(sketch, "E79.18", {"position": v(56.15, -48.18) * mm});
            skArc(sketch, "E79.19", {"start": v(-60, -40.3) * mm, "mid": v(-58.99, -44.68) * mm, "end": v(-56.15, -48.18) * mm});
            skArc(sketch, "E79.20", {"start": v(56.15, -48.18) * mm, "mid": v(58.99, -44.68) * mm, "end": v(60, -40.3) * mm});
            skLineSegment(sketch, "E80", {"start": v(-27.97, 90) * mm, "end": v(-11.96, 108) * mm});
            skLineSegment(sketch, "E81", {"start": v(-11.96, 108) * mm, "end": v(-11.96, 120) * mm});
            skLineSegment(sketch, "E82", {"start": v(36.04, 90) * mm, "end": v(18.04, 108) * mm});
            skLineSegment(sketch, "E83", {"start": v(18.04, 108) * mm, "end": v(18.04, 120) * mm});
            skArc(sketch, "E84", {"start": v(18.04, 120) * mm, "mid": v(3.04, 135) * mm, "end": v(-11.96, 120) * mm});
            skCircle(sketch, "E85", {"center": v(3.04, 120) * mm, "radius": 6 * mm});
            skLineSegment(sketch, "E86", {"start": v(3.04, 120) * mm, "end": v(3.04, 90) * mm, "construction": true});
            skLineSegment(sketch, "E87", {"start": v(-38.63, 90) * mm, "end": v(-38.63, 84.21) * mm});
            skLineSegment(sketch, "E88", {"start": v(-80, 0) * mm, "end": v(80, 0) * mm, "construction": true});
            skArc(sketch, "E89.MirrorCS", {"start": v(18.04, -120) * mm, "mid": v(3.04, -135) * mm, "end": v(-11.96, -120) * mm});
            skCircle(sketch, "E90.MirrorC", {"center": v(3.04, -120) * mm, "radius": 6 * mm});
            skLineSegment(sketch, "E91.MirrorCS", {"start": v(3.04, -120) * mm, "end": v(3.04, -90) * mm, "construction": true});
            skLineSegment(sketch, "E92.MirrorCS", {"start": v(36.04, -90) * mm, "end": v(18.04, -108) * mm});
            skLineSegment(sketch, "E93.MirrorCS", {"start": v(18.04, -108) * mm, "end": v(18.04, -120) * mm});
            skLineSegment(sketch, "E94.MirrorCS", {"start": v(-27.97, -90) * mm, "end": v(-11.96, -108) * mm});
            skLineSegment(sketch, "E95.MirrorCS", {"start": v(-11.96, -108) * mm, "end": v(-11.96, -120) * mm});
            skSolve(sketch);
        }
        {
            var Q0;
            {var subQ1=sQuery(id+"F16.wireOp",EDGE,"E80");Q0=makeQuery(id+"F16.imprint","IMPRINT",FACE,{"disambiguationData":[TD([[makeQuery(id+"F16.imprint","IMPRINT",EDGE,{"derivedFrom":subQ1}),-1.0]])]});}
            var Q1;
            {var subQ4=sQuery(id+"F16.wireOp",EDGE,"E79.1");Q1=makeQuery(id+"F16.imprint","IMPRINT",FACE,{"disambiguationData":[TD([[makeQuery(id+"F16.imprint","IMPRINT",EDGE,{"derivedFrom":subQ4}),1.0]])]});}
            var Q2;
            Q2=makeQuery(id+"F16.imprint","IMPRINT",FACE,{"disambiguationData":[TD([[makeQuery(id+"F16.imprint","IMPRINT",EDGE,{"derivedFrom":sQuery(id+"F16.wireOp",EDGE,"E89.MirrorCS")}),-1.0]])]});
            var Q3;
            Q3=makeQuery(id+"F2.opExtrude","CAP_FACE",FACE,{"disambiguationData":[OSD([sQuery(id+"F0.wireOp",EDGE,"E12"),sQuery(id+"F0.wireOp",EDGE,"E13"),sQuery(id+"F0.wireOp",EDGE,"E14"),sQuery(id+"F0.wireOp",EDGE,"E15"),sQuery(id+"F0.wireOp",EDGE,"E17.filletArc"),sQuery(id+"F0.wireOp",EDGE,"E18.filletArc"),sQuery(id+"F0.wireOp",EDGE,"E19.filletArc"),sQuery(id+"F0.wireOp",EDGE,"E20.filletArc"),sQuery(id+"F0.wireOp",EDGE,"E25.0"),sQuery(id+"F0.wireOp",EDGE,"E25.1"),sQuery(id+"F0.wireOp",EDGE,"E25.2"),sQuery(id+"F0.wireOp",EDGE,"E25.3"),sQuery(id+"F0.wireOp",EDGE,"E25.4"),sQuery(id+"F0.wireOp",EDGE,"E25.5"),sQuery(id+"F0.wireOp",EDGE,"E25.6"),sQuery(id+"F0.wireOp",EDGE,"E25.7")])],"isStart":false});
            extrude(context, id + "F17", {"entities" : qUnion([Q0, Q1, Q2]), "endBound" : BoundingType.UP_TO_SURFACE, "depth" : 25 * mm, "endBoundEntityFace" : qUnion([Q3]), "offsetDistance" : 25 * mm});
        }
    });
